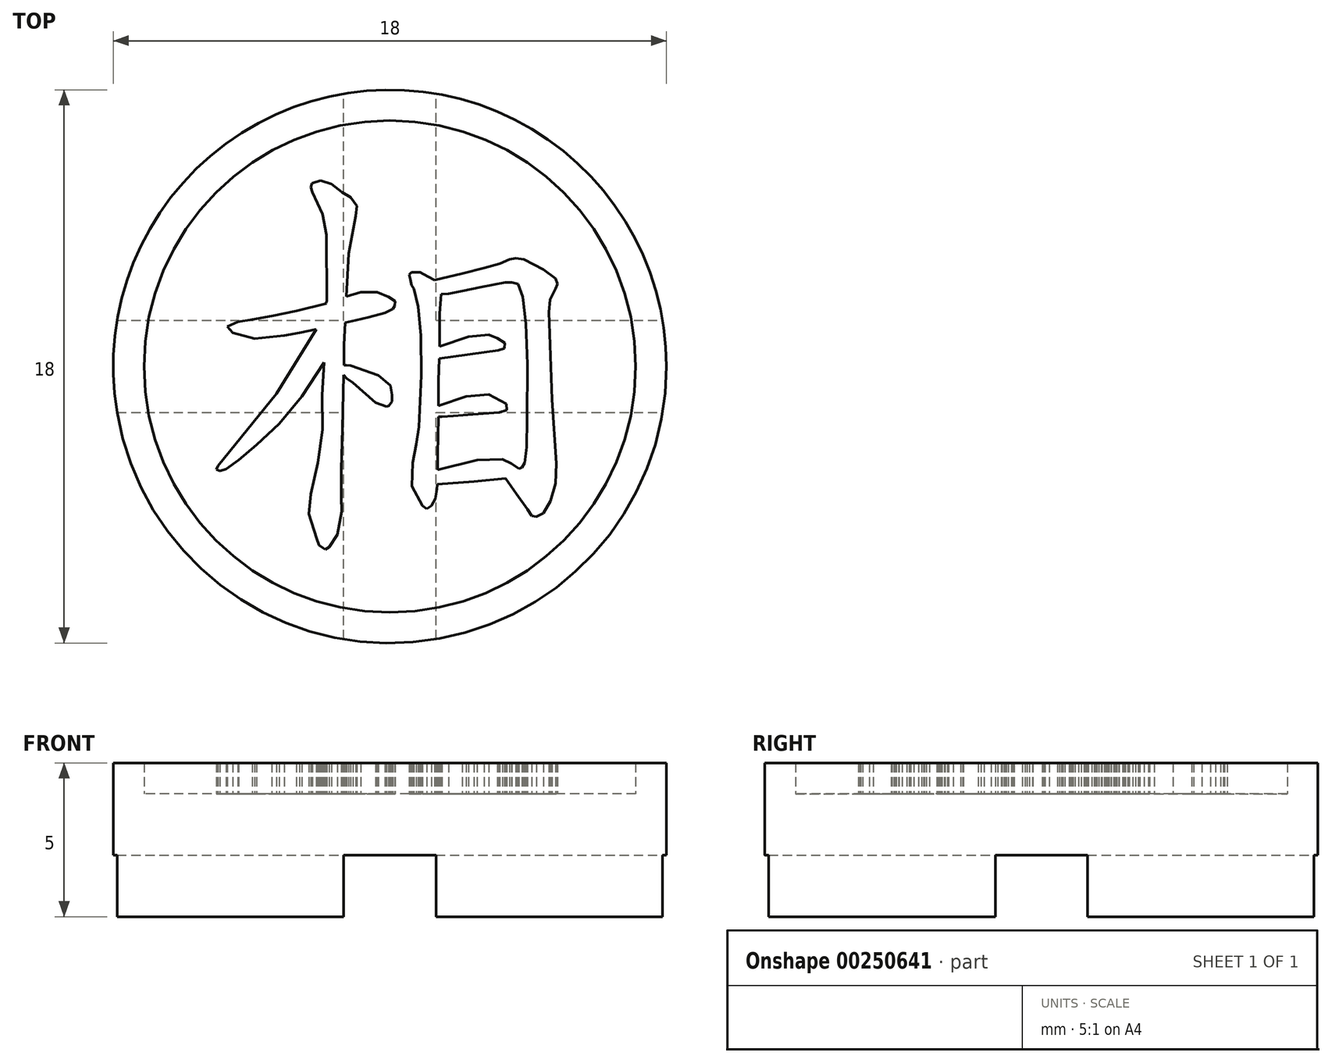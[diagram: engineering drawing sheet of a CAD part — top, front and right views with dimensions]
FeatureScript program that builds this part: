
annotation { "Feature Type Name" : "Feature", "Feature Type Description" : "" }
export const myFeature = defineFeature(function(context is Context, id is Id, definition is map)
    precondition{}
    {
        {
            var Q0;
            Q0=qCreatedBy(makeId("Top.planeOp"),FACE);
            var sketch = newSketch(context, id + "F0", { "sketchPlane" : qUnion([Q0])});
            skCircle(sketch, "E0", {"center": v(-31.33, 19.76) * mm, "radius": 9 * mm});
            skSolve(sketch);
        }
        {
            var Q0;
            Q0=qSketchRegion(id+"F0",true);
            extrude(context, id + "F1", {"entities" : qUnion([Q0]), "depth" : 4 * mm});
        }
        {
            var Q0;
            Q0=makeQuery(id+"F1.opExtrude","CAP_FACE",FACE,{"disambiguationData":[OSD([sQuery(id+"F0.wireOp",EDGE,"E0")])],"isStart":false});
            var sketch = newSketch(context, id + "F2", { "sketchPlane" : qUnion([Q0])});
            skCircle(sketch, "E1", {"center": v(-31.33, 19.76) * mm, "radius": 8 * mm});
            skCircle(sketch, "E2", {"center": v(-31.33, 19.76) * mm, "radius": 9 * mm});
            skSolve(sketch);
        }
        {
            var Q0;
            Q0=makeQuery(id+"F1.opExtrude","CAP_FACE",FACE,{"disambiguationData":[OSD([sQuery(id+"F0.wireOp",EDGE,"E0")])],"isStart":true});
            var sketch = newSketch(context, id + "F3", { "sketchPlane" : qUnion([Q0])});
            skLineSegment(sketch, "E3", {"start": v(-31.33, -19.76) * mm, "end": v(-22.33, -19.76) * mm, "construction": true});
            skLineSegment(sketch, "E4", {"start": v(-31.33, -19.76) * mm, "end": v(-31.33, -10.76) * mm, "construction": true});
            skLineSegment(sketch, "E5", {"start": v(-31.33, -19.76) * mm, "end": v(-40.33, -19.76) * mm, "construction": true});
            skLineSegment(sketch, "E6", {"start": v(-31.33, -19.76) * mm, "end": v(-31.33, -28.76) * mm, "construction": true});
            skLineSegment(sketch, "E7.bottom", {"start": v(-40.33, -28.76) * mm, "end": v(-22.33, -28.76) * mm});
            skLineSegment(sketch, "E7.top", {"start": v(-40.33, -10.76) * mm, "end": v(-22.33, -10.76) * mm});
            skLineSegment(sketch, "E7.left", {"start": v(-22.33, -10.76) * mm, "end": v(-22.33, -28.76) * mm});
            skLineSegment(sketch, "E7.right", {"start": v(-40.33, -10.76) * mm, "end": v(-40.33, -28.76) * mm});
            skPoint(sketch, "E8", {"position": v(-31.33, -28.76) * mm});
            skPoint(sketch, "E9", {"position": v(-40.33, -19.76) * mm});
            skPoint(sketch, "E10", {"position": v(-22.33, -19.76) * mm});
            skPoint(sketch, "E11", {"position": v(-31.33, -10.76) * mm});
            skLineSegment(sketch, "E12.bottom", {"start": v(-32.83, -10.76) * mm, "end": v(-29.83, -10.76) * mm});
            skLineSegment(sketch, "E12.top", {"start": v(-32.83, -28.76) * mm, "end": v(-29.83, -28.76) * mm});
            skLineSegment(sketch, "E12.left", {"start": v(-32.83, -10.76) * mm, "end": v(-32.83, -28.76) * mm});
            skLineSegment(sketch, "E12.right", {"start": v(-29.83, -10.76) * mm, "end": v(-29.83, -28.76) * mm});
            skLineSegment(sketch, "E13.bottom", {"start": v(-40.33, -18.26) * mm, "end": v(-22.33, -18.26) * mm});
            skLineSegment(sketch, "E13.top", {"start": v(-40.33, -21.26) * mm, "end": v(-22.33, -21.26) * mm});
            skLineSegment(sketch, "E13.left", {"start": v(-40.33, -18.26) * mm, "end": v(-40.33, -21.26) * mm});
            skLineSegment(sketch, "E13.right", {"start": v(-22.33, -18.26) * mm, "end": v(-22.33, -21.26) * mm});
            skSolve(sketch);
        }
        {
            var Q0;
            {var subQ1=sQuery(id+"F3.wireOp",EDGE,"E12.bottom");var subQ3=makeQuery(id+"F1.opExtrude","CAP_EDGE",EDGE,{"disambiguationData":[OSD([sQuery(id+"F0.wireOp",EDGE,"E0")])],"isStart":true});var subQ4=makeQuery(id+"F3.imprint","INTERSECT",VERTEX,{"derivedFrom":[subQ3,subQ1]});Q0=makeQuery(id+"F3.imprint","IMPRINT",FACE,{"disambiguationData":[TD([[makeQuery(id+"F3.imprint","IMPRINT",EDGE,{"disambiguationData":[TD([[subQ4,1.0]])],"derivedFrom":subQ3}),1.0]])]});}
            var Q1;
            {var subQ1=sQuery(id+"F3.wireOp",EDGE,"E12.bottom");var subQ3=makeQuery(id+"F1.opExtrude","CAP_EDGE",EDGE,{"disambiguationData":[OSD([sQuery(id+"F0.wireOp",EDGE,"E0")])],"isStart":true});var subQ4=makeQuery(id+"F3.imprint","INTERSECT",VERTEX,{"derivedFrom":[subQ3,subQ1]});Q1=makeQuery(id+"F3.imprint","IMPRINT",FACE,{"disambiguationData":[TD([[makeQuery(id+"F3.imprint","IMPRINT",EDGE,{"disambiguationData":[TD([[subQ4,-1.0]])],"derivedFrom":subQ3}),1.0]])]});}
            var Q2;
            {var subQ1=sQuery(id+"F3.wireOp",EDGE,"E12.top");var subQ3=makeQuery(id+"F1.opExtrude","CAP_EDGE",EDGE,{"disambiguationData":[OSD([sQuery(id+"F0.wireOp",EDGE,"E0")])],"isStart":true});var subQ4=makeQuery(id+"F3.imprint","INTERSECT",VERTEX,{"derivedFrom":[subQ3,subQ1]});Q2=makeQuery(id+"F3.imprint","IMPRINT",FACE,{"disambiguationData":[TD([[makeQuery(id+"F3.imprint","IMPRINT",EDGE,{"disambiguationData":[TD([[subQ4,-1.0]])],"derivedFrom":subQ3}),1.0]])]});}
            var Q3;
            {var subQ1=sQuery(id+"F3.wireOp",EDGE,"E12.top");var subQ3=makeQuery(id+"F1.opExtrude","CAP_EDGE",EDGE,{"disambiguationData":[OSD([sQuery(id+"F0.wireOp",EDGE,"E0")])],"isStart":true});var subQ4=makeQuery(id+"F3.imprint","INTERSECT",VERTEX,{"derivedFrom":[subQ3,subQ1]});Q3=makeQuery(id+"F3.imprint","IMPRINT",FACE,{"disambiguationData":[TD([[makeQuery(id+"F3.imprint","IMPRINT",EDGE,{"disambiguationData":[TD([[subQ4,1.0]])],"derivedFrom":subQ3}),1.0]])]});}
            var Q4;
            {var subQ0=sQuery(id+"F3.wireOp",EDGE,"E13.left");var subQ3=makeQuery(id+"F1.opExtrude","CAP_EDGE",EDGE,{"disambiguationData":[OSD([sQuery(id+"F0.wireOp",EDGE,"E0")])],"isStart":true});var subQ5=makeQuery(id+"F3.imprint","INTERSECT",VERTEX,{"derivedFrom":[subQ3,subQ0]});Q4=makeQuery(id+"F3.imprint","IMPRINT",FACE,{"disambiguationData":[TD([[makeQuery(id+"F3.imprint","IMPRINT",EDGE,{"disambiguationData":[TD([[subQ5,-1.0]])],"derivedFrom":subQ3}),1.0]])]});}
            var Q5;
            {var subQ0=sQuery(id+"F3.wireOp",EDGE,"E13.right");var subQ3=makeQuery(id+"F1.opExtrude","CAP_EDGE",EDGE,{"disambiguationData":[OSD([sQuery(id+"F0.wireOp",EDGE,"E0")])],"isStart":true});var subQ5=makeQuery(id+"F3.imprint","INTERSECT",VERTEX,{"derivedFrom":[subQ3,subQ0]});Q5=makeQuery(id+"F3.imprint","IMPRINT",FACE,{"disambiguationData":[TD([[makeQuery(id+"F3.imprint","IMPRINT",EDGE,{"disambiguationData":[TD([[subQ5,1.0]])],"derivedFrom":subQ3}),1.0]])]});}
            var Q6;
            {var subQ0=sQuery(id+"F3.wireOp",EDGE,"E13.left");var subQ3=makeQuery(id+"F1.opExtrude","CAP_EDGE",EDGE,{"disambiguationData":[OSD([sQuery(id+"F0.wireOp",EDGE,"E0")])],"isStart":true});var subQ5=makeQuery(id+"F3.imprint","INTERSECT",VERTEX,{"derivedFrom":[subQ3,subQ0]});Q6=makeQuery(id+"F3.imprint","IMPRINT",FACE,{"disambiguationData":[TD([[makeQuery(id+"F3.imprint","IMPRINT",EDGE,{"disambiguationData":[TD([[subQ5,1.0]])],"derivedFrom":subQ3}),1.0]])]});}
            var Q7;
            {var subQ0=sQuery(id+"F3.wireOp",EDGE,"E13.right");var subQ3=makeQuery(id+"F1.opExtrude","CAP_EDGE",EDGE,{"disambiguationData":[OSD([sQuery(id+"F0.wireOp",EDGE,"E0")])],"isStart":true});var subQ5=makeQuery(id+"F3.imprint","INTERSECT",VERTEX,{"derivedFrom":[subQ3,subQ0]});Q7=makeQuery(id+"F3.imprint","IMPRINT",FACE,{"disambiguationData":[TD([[makeQuery(id+"F3.imprint","IMPRINT",EDGE,{"disambiguationData":[TD([[subQ5,-1.0]])],"derivedFrom":subQ3}),1.0]])]});}
            var Q8;
            {var subQ3=makeQuery(id+"F1.opExtrude","CAP_EDGE",EDGE,{"disambiguationData":[OSD([sQuery(id+"F0.wireOp",EDGE,"E0")])],"isStart":true});var subQ5=sQuery(id+"F3.wireOp",EDGE,"E12.left");var subQ8=makeQuery(id+"F3.imprint","INTERSECT",VERTEX,{"disambiguationData":[OD(1.0)],"derivedFrom":[subQ3,subQ5]});Q8=makeQuery(id+"F3.imprint","IMPRINT",FACE,{"disambiguationData":[TD([[makeQuery(id+"F3.imprint","IMPRINT",EDGE,{"disambiguationData":[TD([[subQ8,-1.0]])],"derivedFrom":subQ3}),1.0]])]});}
            var Q9;
            {var subQ3=makeQuery(id+"F1.opExtrude","CAP_EDGE",EDGE,{"disambiguationData":[OSD([sQuery(id+"F0.wireOp",EDGE,"E0")])],"isStart":true});var subQ5=sQuery(id+"F3.wireOp",EDGE,"E12.right");var subQ8=makeQuery(id+"F3.imprint","INTERSECT",VERTEX,{"disambiguationData":[OD(1.0)],"derivedFrom":[subQ3,subQ5]});Q9=makeQuery(id+"F3.imprint","IMPRINT",FACE,{"disambiguationData":[TD([[makeQuery(id+"F3.imprint","IMPRINT",EDGE,{"disambiguationData":[TD([[subQ8,1.0]])],"derivedFrom":subQ3}),1.0]])]});}
            var Q10;
            {var subQ3=makeQuery(id+"F1.opExtrude","CAP_EDGE",EDGE,{"disambiguationData":[OSD([sQuery(id+"F0.wireOp",EDGE,"E0")])],"isStart":true});var subQ5=sQuery(id+"F3.wireOp",EDGE,"E12.left");var subQ8=makeQuery(id+"F3.imprint","INTERSECT",VERTEX,{"disambiguationData":[OD(0.0)],"derivedFrom":[subQ3,subQ5]});Q10=makeQuery(id+"F3.imprint","IMPRINT",FACE,{"disambiguationData":[TD([[makeQuery(id+"F3.imprint","IMPRINT",EDGE,{"disambiguationData":[TD([[subQ8,1.0]])],"derivedFrom":subQ3}),1.0]])]});}
            var Q11;
            {var subQ3=makeQuery(id+"F1.opExtrude","CAP_EDGE",EDGE,{"disambiguationData":[OSD([sQuery(id+"F0.wireOp",EDGE,"E0")])],"isStart":true});var subQ5=sQuery(id+"F3.wireOp",EDGE,"E12.right");var subQ8=makeQuery(id+"F3.imprint","INTERSECT",VERTEX,{"disambiguationData":[OD(0.0)],"derivedFrom":[subQ3,subQ5]});Q11=makeQuery(id+"F3.imprint","IMPRINT",FACE,{"disambiguationData":[TD([[makeQuery(id+"F3.imprint","IMPRINT",EDGE,{"disambiguationData":[TD([[subQ8,-1.0]])],"derivedFrom":subQ3}),1.0]])]});}
            var Q12;
            {var subQ2=sQuery(id+"F3.wireOp",EDGE,"E12.left");var subQ4=sQuery(id+"F3.wireOp",EDGE,"E13.bottom");var subQ8=makeQuery(id+"F3.imprint","INTERSECT",VERTEX,{"derivedFrom":[subQ2,subQ4]});Q12=makeQuery(id+"F3.imprint","IMPRINT",FACE,{"disambiguationData":[TD([[makeQuery(id+"F3.imprint","IMPRINT",EDGE,{"disambiguationData":[TD([[subQ8,1.0]])],"derivedFrom":subQ2}),1.0]])]});}
            var Q13;
            {var subQ1=sQuery(id+"F3.wireOp",EDGE,"E12.left");var subQ5=sQuery(id+"F3.wireOp",EDGE,"E13.bottom");var subQ6=makeQuery(id+"F3.imprint","INTERSECT",VERTEX,{"derivedFrom":[subQ1,subQ5]});Q13=makeQuery(id+"F3.imprint","IMPRINT",FACE,{"disambiguationData":[TD([[makeQuery(id+"F3.imprint","IMPRINT",EDGE,{"disambiguationData":[TD([[subQ6,-1.0]])],"derivedFrom":subQ1}),-1.0]])]});}
            var Q14;
            {var subQ0=sQuery(id+"F3.wireOp",EDGE,"E13.top");var subQ1=sQuery(id+"F3.wireOp",EDGE,"E12.left");var subQ2=makeQuery(id+"F3.imprint","INTERSECT",VERTEX,{"derivedFrom":[subQ1,subQ0]});Q14=makeQuery(id+"F3.imprint","IMPRINT",FACE,{"disambiguationData":[TD([[makeQuery(id+"F3.imprint","IMPRINT",EDGE,{"disambiguationData":[TD([[subQ2,-1.0]])],"derivedFrom":subQ1}),1.0]])]});}
            var Q15;
            {var subQ2=sQuery(id+"F3.wireOp",EDGE,"E13.bottom");var subQ5=sQuery(id+"F3.wireOp",EDGE,"E12.right");var subQ8=makeQuery(id+"F3.imprint","INTERSECT",VERTEX,{"derivedFrom":[subQ5,subQ2]});Q15=makeQuery(id+"F3.imprint","IMPRINT",FACE,{"disambiguationData":[TD([[makeQuery(id+"F3.imprint","IMPRINT",EDGE,{"disambiguationData":[TD([[subQ8,-1.0]])],"derivedFrom":subQ5}),1.0]])]});}
            var Q16;
            {var subQ0=sQuery(id+"F3.wireOp",EDGE,"E13.bottom");var subQ1=sQuery(id+"F3.wireOp",EDGE,"E12.left");var subQ2=makeQuery(id+"F3.imprint","INTERSECT",VERTEX,{"derivedFrom":[subQ1,subQ0]});Q16=makeQuery(id+"F3.imprint","IMPRINT",FACE,{"disambiguationData":[TD([[makeQuery(id+"F3.imprint","IMPRINT",EDGE,{"disambiguationData":[TD([[subQ2,-1.0]])],"derivedFrom":subQ1}),1.0]])]});}
            extrude(context, id + "F4", {"entities" : qUnion([Q0, Q1, Q2, Q3, Q4, Q5, Q6, Q7, Q8, Q9, Q10, Q11, Q12, Q13, Q14, Q15, Q16]), "operationType" : NewBodyOperationType.REMOVE, "oppositeDirection" : true, "depth" : 2 * mm});
        }
        {
            var Q0;
            Q0=qSketchRegion(id+"F2",true);
            var Q1;
            Q1=makeQuery(id+"F2.imprint","IMPRINT",FACE,{"disambiguationData":[TD([[makeQuery(id+"F2.imprint","IMPRINT",EDGE,{"derivedFrom":sQuery(id+"F2.wireOp",EDGE,"hKqnuJLd-dfdz-vJIs-yDKo-c4hLNRw30SuP")}),-1.0]])]});
            extrude(context, id + "F5", {"entities" : qUnion([Q0, Q1]), "operationType" : NewBodyOperationType.ADD, "depth" : 1 * mm});
        }
        {
            var Q0;
            Q0=makeQuery(id+"F1.opExtrude","CAP_FACE",FACE,{"disambiguationData":[OSD([sQuery(id+"F0.wireOp",EDGE,"E0")])],"isStart":false});
            var sketch = newSketch(context, id + "F6", { "sketchPlane" : qUnion([Q0])});
            skLineSegment(sketch, "E14", {"start": v(-32.84, 19.49) * mm, "end": v(-32.73, 19.37) * mm});
            skLineSegment(sketch, "E15", {"start": v(-32.73, 19.37) * mm, "end": v(-32.53, 19.23) * mm});
            skLineSegment(sketch, "E16", {"start": v(-32.53, 19.23) * mm, "end": v(-31.8, 18.58) * mm});
            skLineSegment(sketch, "E17", {"start": v(-31.8, 18.58) * mm, "end": v(-31.44, 18.45) * mm});
            skLineSegment(sketch, "E18", {"start": v(-31.44, 18.45) * mm, "end": v(-31.36, 18.48) * mm});
            skLineSegment(sketch, "E19", {"start": v(-31.36, 18.48) * mm, "end": v(-31.26, 18.63) * mm});
            skLineSegment(sketch, "E20", {"start": v(-31.26, 18.63) * mm, "end": v(-31.27, 18.83) * mm});
            skLineSegment(sketch, "E21", {"start": v(-31.27, 18.83) * mm, "end": v(-31.32, 19.14) * mm});
            skLineSegment(sketch, "E22", {"start": v(-31.32, 19.14) * mm, "end": v(-31.7, 19.47) * mm});
            skLineSegment(sketch, "E23", {"start": v(-31.7, 19.47) * mm, "end": v(-32.6, 19.79) * mm});
            skLineSegment(sketch, "E24", {"start": v(-32.6, 19.79) * mm, "end": v(-32.75, 19.8) * mm});
            skLineSegment(sketch, "E25", {"start": v(-32.75, 19.8) * mm, "end": v(-32.82, 19.8) * mm});
            skLineSegment(sketch, "E26", {"start": v(-32.82, 19.8) * mm, "end": v(-32.83, 20.46) * mm});
            skLineSegment(sketch, "E27", {"start": v(-32.83, 20.46) * mm, "end": v(-32.78, 21.19) * mm});
            skLineSegment(sketch, "E28", {"start": v(-32.78, 21.19) * mm, "end": v(-32.44, 21.26) * mm});
            skLineSegment(sketch, "E29", {"start": v(-32.44, 21.26) * mm, "end": v(-32.01, 21.36) * mm});
            skLineSegment(sketch, "E30", {"start": v(-32.01, 21.36) * mm, "end": v(-31.5, 21.5) * mm});
            skLineSegment(sketch, "E31", {"start": v(-31.5, 21.5) * mm, "end": v(-31.23, 21.63) * mm});
            skLineSegment(sketch, "E32", {"start": v(-31.23, 21.63) * mm, "end": v(-31.17, 21.73) * mm});
            skLineSegment(sketch, "E33", {"start": v(-31.17, 21.73) * mm, "end": v(-31.16, 21.88) * mm});
            skLineSegment(sketch, "E34", {"start": v(-31.16, 21.88) * mm, "end": v(-31.37, 22.02) * mm});
            skLineSegment(sketch, "E35", {"start": v(-31.37, 22.02) * mm, "end": v(-31.74, 22.17) * mm});
            skLineSegment(sketch, "E36", {"start": v(-31.74, 22.17) * mm, "end": v(-32.28, 22.18) * mm});
            skLineSegment(sketch, "E37", {"start": v(-32.28, 22.18) * mm, "end": v(-32.75, 22.04) * mm});
            skLineSegment(sketch, "E38", {"start": v(-32.75, 22.04) * mm, "end": v(-32.67, 23.43) * mm});
            skLineSegment(sketch, "E39", {"start": v(-32.67, 23.43) * mm, "end": v(-32.44, 24.65) * mm});
            skLineSegment(sketch, "E40", {"start": v(-32.44, 24.65) * mm, "end": v(-32.4, 24.99) * mm});
            skLineSegment(sketch, "E41", {"start": v(-32.4, 24.99) * mm, "end": v(-32.6, 25.26) * mm});
            skLineSegment(sketch, "E42", {"start": v(-32.6, 25.26) * mm, "end": v(-32.9, 25.43) * mm});
            skLineSegment(sketch, "E43", {"start": v(-32.9, 25.43) * mm, "end": v(-33.23, 25.69) * mm});
            skLineSegment(sketch, "E44", {"start": v(-33.23, 25.69) * mm, "end": v(-33.59, 25.8) * mm});
            skLineSegment(sketch, "E45", {"start": v(-33.59, 25.8) * mm, "end": v(-33.86, 25.71) * mm});
            skLineSegment(sketch, "E46", {"start": v(-33.86, 25.71) * mm, "end": v(-33.9, 25.6) * mm});
            skLineSegment(sketch, "E47", {"start": v(-33.9, 25.6) * mm, "end": v(-33.85, 25.43) * mm});
            skLineSegment(sketch, "E48", {"start": v(-33.85, 25.43) * mm, "end": v(-33.52, 24.72) * mm});
            skLineSegment(sketch, "E49", {"start": v(-33.52, 24.72) * mm, "end": v(-33.4, 24.04) * mm});
            skLineSegment(sketch, "E50", {"start": v(-33.4, 24.04) * mm, "end": v(-33.38, 21.88) * mm});
            skLineSegment(sketch, "E51", {"start": v(-33.38, 21.88) * mm, "end": v(-33.4, 21.83) * mm});
            skLineSegment(sketch, "E52", {"start": v(-33.4, 21.83) * mm, "end": v(-33.4, 21.8) * mm});
            skLineSegment(sketch, "E53", {"start": v(-33.4, 21.8) * mm, "end": v(-34.37, 21.56) * mm});
            skLineSegment(sketch, "E54", {"start": v(-34.37, 21.56) * mm, "end": v(-35.17, 21.4) * mm});
            skLineSegment(sketch, "E55", {"start": v(-35.17, 21.4) * mm, "end": v(-35.8, 21.28) * mm});
            skLineSegment(sketch, "E56", {"start": v(-35.8, 21.28) * mm, "end": v(-36.27, 21.21) * mm});
            skLineSegment(sketch, "E57", {"start": v(-36.27, 21.21) * mm, "end": v(-36.62, 21.05) * mm});
            skLineSegment(sketch, "E58", {"start": v(-36.62, 21.05) * mm, "end": v(-36.44, 20.86) * mm});
            skLineSegment(sketch, "E59", {"start": v(-36.44, 20.86) * mm, "end": v(-35.73, 20.66) * mm});
            skLineSegment(sketch, "E60", {"start": v(-35.73, 20.66) * mm, "end": v(-34.77, 20.76) * mm});
            skLineSegment(sketch, "E61", {"start": v(-34.77, 20.76) * mm, "end": v(-34.27, 20.85) * mm});
            skLineSegment(sketch, "E62", {"start": v(-34.27, 20.85) * mm, "end": v(-33.73, 20.97) * mm});
            skLineSegment(sketch, "E63", {"start": v(-33.73, 20.97) * mm, "end": v(-35.02, 18.87) * mm});
            skLineSegment(sketch, "E64", {"start": v(-35.02, 18.87) * mm, "end": v(-36.93, 16.53) * mm});
            skLineSegment(sketch, "E65", {"start": v(-36.93, 16.53) * mm, "end": v(-36.98, 16.41) * mm});
            skLineSegment(sketch, "E66", {"start": v(-36.98, 16.41) * mm, "end": v(-36.86, 16.35) * mm});
            skLineSegment(sketch, "E67", {"start": v(-36.86, 16.35) * mm, "end": v(-36.66, 16.42) * mm});
            skLineSegment(sketch, "E68", {"start": v(-36.66, 16.42) * mm, "end": v(-36.25, 16.7) * mm});
            skLineSegment(sketch, "E69", {"start": v(-36.25, 16.7) * mm, "end": v(-35.67, 17.2) * mm});
            skLineSegment(sketch, "E70", {"start": v(-35.67, 17.2) * mm, "end": v(-34.93, 17.9) * mm});
            skLineSegment(sketch, "E71", {"start": v(-34.93, 17.9) * mm, "end": v(-34.2, 18.78) * mm});
            skLineSegment(sketch, "E72", {"start": v(-34.2, 18.78) * mm, "end": v(-33.47, 19.88) * mm});
            skLineSegment(sketch, "E73", {"start": v(-33.47, 19.88) * mm, "end": v(-33.53, 18.82) * mm});
            skLineSegment(sketch, "E74", {"start": v(-33.53, 18.82) * mm, "end": v(-33.52, 17.7) * mm});
            skLineSegment(sketch, "E75", {"start": v(-33.52, 17.7) * mm, "end": v(-33.68, 16.63) * mm});
            skLineSegment(sketch, "E76", {"start": v(-33.68, 16.63) * mm, "end": v(-33.9, 15.61) * mm});
            skLineSegment(sketch, "E77", {"start": v(-33.9, 15.61) * mm, "end": v(-33.96, 14.96) * mm});
            skLineSegment(sketch, "E78", {"start": v(-33.96, 14.96) * mm, "end": v(-33.71, 14.16) * mm});
            skLineSegment(sketch, "E79", {"start": v(-33.71, 14.16) * mm, "end": v(-33.64, 13.94) * mm});
            skLineSegment(sketch, "E80", {"start": v(-33.64, 13.94) * mm, "end": v(-33.5, 13.86) * mm});
            skLineSegment(sketch, "E81", {"start": v(-33.5, 13.86) * mm, "end": v(-33.43, 13.8) * mm});
            skLineSegment(sketch, "E82", {"start": v(-33.43, 13.8) * mm, "end": v(-33.3, 13.89) * mm});
            skLineSegment(sketch, "E83", {"start": v(-33.3, 13.89) * mm, "end": v(-33.04, 14.28) * mm});
            skLineSegment(sketch, "E84", {"start": v(-33.04, 14.28) * mm, "end": v(-32.9, 15.04) * mm});
            skLineSegment(sketch, "E85", {"start": v(-32.9, 15.04) * mm, "end": v(-32.92, 15.5) * mm});
            skLineSegment(sketch, "E86", {"start": v(-32.92, 15.5) * mm, "end": v(-32.9, 16.4) * mm});
            skLineSegment(sketch, "E87", {"start": v(-32.9, 16.4) * mm, "end": v(-32.88, 17.74) * mm});
            skLineSegment(sketch, "E88", {"start": v(-32.88, 17.74) * mm, "end": v(-32.84, 19.49) * mm});
            skLineSegment(sketch, "E89", {"start": v(-29.78, 15.93) * mm, "end": v(-28.6, 16.02) * mm});
            skLineSegment(sketch, "E90", {"start": v(-28.6, 16.02) * mm, "end": v(-27.57, 16.12) * mm});
            skLineSegment(sketch, "E91", {"start": v(-27.57, 16.12) * mm, "end": v(-27.21, 15.6) * mm});
            skLineSegment(sketch, "E92", {"start": v(-27.21, 15.6) * mm, "end": v(-26.85, 15.12) * mm});
            skLineSegment(sketch, "E93", {"start": v(-26.85, 15.12) * mm, "end": v(-26.72, 14.9) * mm});
            skLineSegment(sketch, "E94", {"start": v(-26.72, 14.9) * mm, "end": v(-26.57, 14.87) * mm});
            skLineSegment(sketch, "E95", {"start": v(-26.57, 14.87) * mm, "end": v(-26.34, 14.98) * mm});
            skLineSegment(sketch, "E96", {"start": v(-26.34, 14.98) * mm, "end": v(-26.1, 15.38) * mm});
            skLineSegment(sketch, "E97", {"start": v(-26.1, 15.38) * mm, "end": v(-25.94, 15.96) * mm});
            skLineSegment(sketch, "E98", {"start": v(-25.94, 15.96) * mm, "end": v(-25.9, 16.6) * mm});
            skLineSegment(sketch, "E99", {"start": v(-25.9, 16.6) * mm, "end": v(-26.05, 18.69) * mm});
            skLineSegment(sketch, "E100", {"start": v(-26.05, 18.69) * mm, "end": v(-26.16, 21.53) * mm});
            skLineSegment(sketch, "E101", {"start": v(-26.16, 21.53) * mm, "end": v(-26.11, 21.94) * mm});
            skLineSegment(sketch, "E102", {"start": v(-26.11, 21.94) * mm, "end": v(-25.94, 22.3) * mm});
            skLineSegment(sketch, "E103", {"start": v(-25.94, 22.3) * mm, "end": v(-25.87, 22.45) * mm});
            skLineSegment(sketch, "E104", {"start": v(-25.87, 22.45) * mm, "end": v(-25.94, 22.62) * mm});
            skLineSegment(sketch, "E105", {"start": v(-25.94, 22.62) * mm, "end": v(-26.33, 22.92) * mm});
            skLineSegment(sketch, "E106", {"start": v(-26.33, 22.92) * mm, "end": v(-26.96, 23.24) * mm});
            skLineSegment(sketch, "E107", {"start": v(-26.96, 23.24) * mm, "end": v(-27.23, 23.28) * mm});
            skLineSegment(sketch, "E108", {"start": v(-27.23, 23.28) * mm, "end": v(-27.44, 23.24) * mm});
            skLineSegment(sketch, "E109", {"start": v(-27.44, 23.24) * mm, "end": v(-27.75, 23.1) * mm});
            skLineSegment(sketch, "E110", {"start": v(-27.75, 23.1) * mm, "end": v(-28.26, 22.96) * mm});
            skLineSegment(sketch, "E111", {"start": v(-28.26, 22.96) * mm, "end": v(-28.96, 22.79) * mm});
            skLineSegment(sketch, "E112", {"start": v(-28.96, 22.79) * mm, "end": v(-29.88, 22.57) * mm});
            skLineSegment(sketch, "E113", {"start": v(-29.88, 22.57) * mm, "end": v(-30.1, 22.69) * mm});
            skLineSegment(sketch, "E114", {"start": v(-30.1, 22.69) * mm, "end": v(-30.34, 22.83) * mm});
            skLineSegment(sketch, "E115", {"start": v(-30.34, 22.83) * mm, "end": v(-30.63, 22.83) * mm});
            skLineSegment(sketch, "E116", {"start": v(-30.63, 22.83) * mm, "end": v(-30.7, 22.74) * mm});
            skLineSegment(sketch, "E117", {"start": v(-30.7, 22.74) * mm, "end": v(-30.66, 22.6) * mm});
            skLineSegment(sketch, "E118", {"start": v(-30.66, 22.6) * mm, "end": v(-30.62, 22.4) * mm});
            skLineSegment(sketch, "E119", {"start": v(-30.62, 22.4) * mm, "end": v(-30.55, 22.28) * mm});
            skLineSegment(sketch, "E120", {"start": v(-30.55, 22.28) * mm, "end": v(-30.41, 21.7) * mm});
            skLineSegment(sketch, "E121", {"start": v(-30.41, 21.7) * mm, "end": v(-30.32, 20.77) * mm});
            skLineSegment(sketch, "E122", {"start": v(-30.32, 20.77) * mm, "end": v(-30.31, 19.47) * mm});
            skLineSegment(sketch, "E123", {"start": v(-30.31, 19.47) * mm, "end": v(-30.38, 17.8) * mm});
            skLineSegment(sketch, "E124", {"start": v(-30.38, 17.8) * mm, "end": v(-30.48, 17.22) * mm});
            skLineSegment(sketch, "E125", {"start": v(-30.48, 17.22) * mm, "end": v(-30.59, 16.62) * mm});
            skLineSegment(sketch, "E126", {"start": v(-30.59, 16.62) * mm, "end": v(-30.62, 15.87) * mm});
            skLineSegment(sketch, "E127", {"start": v(-30.62, 15.87) * mm, "end": v(-30.27, 15.23) * mm});
            skLineSegment(sketch, "E128", {"start": v(-30.27, 15.23) * mm, "end": v(-30.13, 15.13) * mm});
            skLineSegment(sketch, "E129", {"start": v(-30.13, 15.13) * mm, "end": v(-29.97, 15.23) * mm});
            skLineSegment(sketch, "E130", {"start": v(-29.97, 15.23) * mm, "end": v(-29.85, 15.46) * mm});
            skLineSegment(sketch, "E131", {"start": v(-29.85, 15.46) * mm, "end": v(-29.8, 15.76) * mm});
            skLineSegment(sketch, "E132", {"start": v(-29.8, 15.76) * mm, "end": v(-29.78, 15.93) * mm});
            skLineSegment(sketch, "E133", {"start": v(-27.66, 16.73) * mm, "end": v(-28.5, 16.7) * mm});
            skLineSegment(sketch, "E134", {"start": v(-28.5, 16.7) * mm, "end": v(-29.77, 16.4) * mm});
            skLineSegment(sketch, "E135", {"start": v(-29.77, 16.4) * mm, "end": v(-29.77, 16.9) * mm});
            skLineSegment(sketch, "E136", {"start": v(-29.77, 16.9) * mm, "end": v(-29.75, 18.12) * mm});
            skLineSegment(sketch, "E137", {"start": v(-29.75, 18.12) * mm, "end": v(-29.64, 18.12) * mm});
            skLineSegment(sketch, "E138", {"start": v(-29.64, 18.12) * mm, "end": v(-29.26, 18.15) * mm});
            skLineSegment(sketch, "E139", {"start": v(-29.26, 18.15) * mm, "end": v(-28.64, 18.2) * mm});
            skLineSegment(sketch, "E140", {"start": v(-28.64, 18.2) * mm, "end": v(-27.77, 18.27) * mm});
            skLineSegment(sketch, "E141", {"start": v(-27.77, 18.27) * mm, "end": v(-27.52, 18.34) * mm});
            skLineSegment(sketch, "E142", {"start": v(-27.52, 18.34) * mm, "end": v(-27.54, 18.54) * mm});
            skLineSegment(sketch, "E143", {"start": v(-27.54, 18.54) * mm, "end": v(-28.11, 18.84) * mm});
            skLineSegment(sketch, "E144", {"start": v(-28.11, 18.84) * mm, "end": v(-28.85, 18.79) * mm});
            skLineSegment(sketch, "E145", {"start": v(-28.85, 18.79) * mm, "end": v(-29.75, 18.47) * mm});
            skLineSegment(sketch, "E146", {"start": v(-29.75, 18.47) * mm, "end": v(-29.75, 19.3) * mm});
            skLineSegment(sketch, "E147", {"start": v(-29.75, 19.3) * mm, "end": v(-29.73, 20.02) * mm});
            skLineSegment(sketch, "E148", {"start": v(-29.73, 20.02) * mm, "end": v(-27.8, 20.28) * mm});
            skLineSegment(sketch, "E149", {"start": v(-27.8, 20.28) * mm, "end": v(-27.6, 20.35) * mm});
            skLineSegment(sketch, "E150", {"start": v(-27.6, 20.35) * mm, "end": v(-27.6, 20.53) * mm});
            skLineSegment(sketch, "E151", {"start": v(-27.6, 20.53) * mm, "end": v(-27.83, 20.67) * mm});
            skLineSegment(sketch, "E152", {"start": v(-27.83, 20.67) * mm, "end": v(-28.11, 20.79) * mm});
            skLineSegment(sketch, "E153", {"start": v(-28.11, 20.79) * mm, "end": v(-28.78, 20.72) * mm});
            skLineSegment(sketch, "E154", {"start": v(-28.78, 20.72) * mm, "end": v(-29.71, 20.4) * mm});
            skLineSegment(sketch, "E155", {"start": v(-29.71, 20.4) * mm, "end": v(-29.7, 21.48) * mm});
            skLineSegment(sketch, "E156", {"start": v(-29.7, 21.48) * mm, "end": v(-29.67, 21.95) * mm});
            skLineSegment(sketch, "E157", {"start": v(-29.67, 21.95) * mm, "end": v(-29.66, 22.12) * mm});
            skLineSegment(sketch, "E158", {"start": v(-29.66, 22.12) * mm, "end": v(-29.41, 22.13) * mm});
            skLineSegment(sketch, "E159", {"start": v(-29.41, 22.13) * mm, "end": v(-28.98, 22.2) * mm});
            skLineSegment(sketch, "E160", {"start": v(-28.98, 22.2) * mm, "end": v(-28.36, 22.34) * mm});
            skLineSegment(sketch, "E161", {"start": v(-28.36, 22.34) * mm, "end": v(-27.58, 22.5) * mm});
            skLineSegment(sketch, "E162", {"start": v(-27.58, 22.5) * mm, "end": v(-27.36, 22.5) * mm});
            skLineSegment(sketch, "E163", {"start": v(-27.36, 22.5) * mm, "end": v(-27.16, 22.45) * mm});
            skLineSegment(sketch, "E164", {"start": v(-27.16, 22.45) * mm, "end": v(-27, 22.02) * mm});
            skLineSegment(sketch, "E165", {"start": v(-27, 22.02) * mm, "end": v(-26.9, 21.15) * mm});
            skLineSegment(sketch, "E166", {"start": v(-26.9, 21.15) * mm, "end": v(-26.85, 19.83) * mm});
            skLineSegment(sketch, "E167", {"start": v(-26.85, 19.83) * mm, "end": v(-26.87, 18.05) * mm});
            skLineSegment(sketch, "E168", {"start": v(-26.87, 18.05) * mm, "end": v(-26.88, 17.13) * mm});
            skLineSegment(sketch, "E169", {"start": v(-26.88, 17.13) * mm, "end": v(-26.95, 16.62) * mm});
            skLineSegment(sketch, "E170", {"start": v(-26.95, 16.62) * mm, "end": v(-27.03, 16.48) * mm});
            skLineSegment(sketch, "E171", {"start": v(-27.03, 16.48) * mm, "end": v(-27.13, 16.43) * mm});
            skLineSegment(sketch, "E172", {"start": v(-27.13, 16.43) * mm, "end": v(-27.37, 16.6) * mm});
            skLineSegment(sketch, "E173", {"start": v(-27.37, 16.6) * mm, "end": v(-27.66, 16.73) * mm});
            skSolve(sketch);
        }
        {
            var Q0;
            Q0 = qSketchRegion(id + "F6", true);
            extrude(context, id + "F7", {"entities" : qUnion([Q0]), "operationType" : NewBodyOperationType.ADD, "depth" : 1 * mm, "offsetDistance" : 25 * mm});
        }
    });
